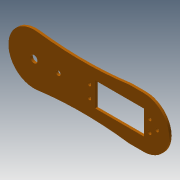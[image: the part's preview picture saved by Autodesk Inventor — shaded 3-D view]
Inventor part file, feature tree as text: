
AUTODESK INVENTOR PART (.ipt)
format: ipt  version: 2013 (Build 170138000, 138)  size: 128,512 bytes
history: native  units: mm
features: extrude x3, sketch x3
ambient origin geometry x8: Origin, YZ Plane, XZ Plane, XY Plane, X Axis, Y Axis, Z Axis, Center Point
bodies: Solid1 (feature_tree)
feature tree (6):
  extrude  "Extrusion1"  Depth=40.2mm
  extrude  "Extrusion2"  Depth=20.0mm
  extrude  "Extrusion3"  Depth=6.0mm
  sketch  "Sketch1"  dims[d2=42.0mm d11=40.2mm]
  sketch  "Sketch2"  dims[d13=55.0mm d14=20.0mm]
  sketch  "Sketch3"  dims[d23=3.0mm d24=6.0mm d25=40.0mm d26=10.0mm d27=3.0mm d28=40.0mm d29=4.0mm d30=2.0mm d31=0.0mm d32=2.0mm d33=0.0mm d34=20.0mm d35=4.0mm d36=2.0mm d37=0.0mm]
